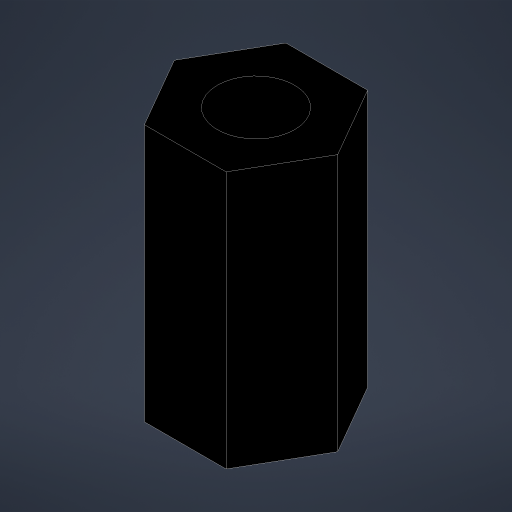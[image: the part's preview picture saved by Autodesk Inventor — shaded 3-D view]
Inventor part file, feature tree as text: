
AUTODESK INVENTOR PART (.ipt)
format: ipt  version: 2024.1 (Build 281209000, 209)  size: 159,232 bytes
history: native  units: mm
features: extrude x1, sketch x1
ambient origin geometry x8: Origin, YZ Plane, XZ Plane, XY Plane, X Axis, Y Axis, Z Axis, Center Point
bodies: Solid1 (feature_tree)
feature tree (2):
  extrude  "Extrusion1"  Depth=10.0mm
  sketch  "Sketch1"  dims[d0=5.5mm d1=3.0mm d2=10.0mm d3=0.0mm d4=0.5mm d5=0.872665mm]
